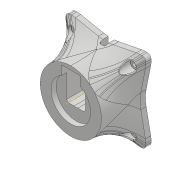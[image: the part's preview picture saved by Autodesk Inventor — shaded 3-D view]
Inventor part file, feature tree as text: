
AUTODESK INVENTOR PART (.ipt)
format: ipt  version: 2018 (Build 220112000, 112)  size: 1,944,576 bytes
history: native  units: mm
features: sketch x37, projected_geometry x36, extrude x32, fillet x13, hole x4, chamfer x4, mirror x1, other x1, revolve x1, shell x1, pattern_circular x1
ambient origin geometry x8: Origin, YZ Plane, XZ Plane, XY Plane, X Axis, Y Axis, Z Axis, Center Point
bodies: Solid1 (feature_tree)
feature tree (131):
  extrude  "Extrusion1"  Depth=45.0mm
  extrude  "Extrusion2"  Depth=2.25mm
  hole  "Hole1"  [1 undecoded]
  hole  "Hole2"  [1 undecoded]
  fillet  "Fillet1"  Radius=14.0mm
  extrude  "Extrusion3"  Depth=18.5mm
  extrude  "Extrusion4"  Depth=10.0mm
  extrude  "Extrusion5"  Depth=2.195mm
  extrude  "Extrusion6"  Depth=20.5mm
  hole  "Hole3"  [1 undecoded]
  extrude  "Extrusion7"  Depth=0.5mm
  extrude  "Extrusion8"  Depth=5.0mm TaperAngle=0.0deg
  extrude  "Extrusion9"  Depth=10.0mm
  extrude  "Extrusion10"  Depth=10.0mm
  extrude  "Extrusion11"  Depth=14.5mm
  extrude  "Extrusion12"  Depth=14.5mm
  extrude  "Extrusion13"  Depth=5.0mm
  extrude  "Extrusion14"  Depth=2.25mm
  extrude  "Extrusion15"  Depth=5.0mm
  extrude  "Extrusion16"  Depth=9.0mm
  extrude  "Extrusion17"  Depth=4.0mm
  chamfer  "Chamfer1"  Distance=1.0mm
  fillet  "Fillet7"  Radius=20.7mm
  fillet  "Fillet8"  Radius=32.0mm
  mirror  "Mirror1"
  extrude  "Extrusion18"  Depth=1.0mm TaperAngle=0.0deg
  extrude  "Extrusion19"  Depth=8.0mm
  extrude  "Extrusion20"  Depth=0.2mm TaperAngle=0.0deg
  extrude  "Extrusion21"  Depth=0.5mm TaperAngle=0.0deg
  extrude  "Extrusion22"  Depth=3.0mm TaperAngle=0.0deg
  extrude  "Extrusion23"  Depth=0.2mm TaperAngle=0.0deg
  extrude  "Extrusion24"  Depth=2.5mm TaperAngle=45.0deg
  sketch  "Sketch35"  dims[d91=8.0mm d92=0.0mm d93=3.0mm d94=0.0mm]
  other  "Work Axis1"
  revolve  "Revolution1"  [1 undecoded]
  extrude  "Extrusion25"  Depth=4.0mm TaperAngle=0.0deg
  extrude  "Extrusion26"  Depth=19.2mm TaperAngle=0.0deg
  shell  "Shell1"  Thickness=52.1mm
  extrude  "Extrusion27"  Depth=9.0mm
  extrude  "Extrusion28"  Depth=25.0mm
  chamfer  "Chamfer4"  Distance=6.9mm
  chamfer  "Chamfer5"  Distance=5.2mm
  extrude  "Extrusion29"  Depth=5.2mm
  pattern_circular  "Circular Pattern1"  [2 undecoded]
  fillet  "Fillet11"  Radius=5.0mm
  fillet  "Fillet12"  [1 undecoded]
  fillet  "Fillet13"  Radius=5.0mm
  fillet  "Fillet14"  Radius=105.0mm
  chamfer  "Chamfer6"  Distance=105.0mm
  hole  "Hole6"  [1 undecoded]
  extrude  "Extrusion30"  Depth=0.3mm
  fillet  "Fillet15"  Radius=12.8mm
  extrude  "Extrusion31"  Depth=0.3mm
  fillet  "Fillet16"  Radius=12.8mm
  extrude  "Extrusion32"  Depth=0.3mm
  fillet  "Fillet17"  Radius=20.0mm
  fillet  "Fillet18"  Radius=20.0mm
  fillet  "Fillet19"  Radius=6.0mm
  fillet  "Fillet20"  Radius=40.0mm
  sketch  "Sketch1"  dims[d0=24.5mm d1=45.0mm]
  sketch  "Sketch2"  dims[d2=1.95mm d3=0.0mm d4=2.25mm]
  projected_geometry  "Projected Loop1"
  sketch  "Sketch3"  dims[d5=20.0mm d6=2.25mm]
  projected_geometry  "Projected Loop2"
  sketch  "Sketch4"  dims[d7=5.25mm d8=5.25mm d9=14.0mm]
  projected_geometry  "Projected Loop3"
  sketch  "Sketch5"  dims[d10=5.25mm d11=18.5mm]
  projected_geometry  "Projected Loop4"
  sketch  "Sketch6"  dims[d12=10.0mm d13=0.0mm d14=20.5mm]
  projected_geometry  "Projected Loop5"
  sketch  "Sketch7"  dims[d15=2.0mm d16=2.195mm]
  projected_geometry  "Projected Loop6"
  sketch  "Sketch8"  dims[d17=2.0mm]
  projected_geometry  "Projected Loop7"
  sketch  "Sketch9"  dims[d18=2.4mm d19=6.0mm d20=4.4mm d21=2.0mm d22=90.0deg d23=8.0mm d24=20.594885mm d25=20.5mm]
  projected_geometry  "Projected Loop8"
  projected_geometry  "Projected Loop9"
  sketch  "Sketch10"  dims[d26=26.65mm d27=2.0mm]
  projected_geometry  "Projected Loop10"
  projected_geometry  "Projected Loop11"
  sketch  "Sketch11"  dims[d28=2.0mm]
  projected_geometry  "Projected Loop12"
  sketch  "Sketch12"  dims[d29=2.4mm d30=6.0mm d31=4.4mm d32=2.0mm d33=90.0deg d34=8.0mm d35=20.594885mm d36=0.5mm]
  sketch  "Sketch13"  dims[d37=18.0mm d38=5.0mm d39=0.0mm]
  sketch  "Sketch14"  dims[d41=10.0mm d42=0.0mm d43=24.5mm]
  projected_geometry  "Projected Loop13"
  sketch  "Sketch15"  dims[d44=1.15mm d45=0.0mm d46=10.0mm]
  sketch  "Sketch16"  dims[d47=21.0mm d48=14.5mm]
  projected_geometry  "Projected Loop14"
  sketch  "Sketch17"  dims[d49=20.0mm d50=14.5mm]
  projected_geometry  "Projected Loop15"
  sketch  "Sketch18"  dims[d51=24.5mm d52=5.0mm]
  projected_geometry  "Projected Loop16"
  sketch  "Sketch19"  dims[d53=5.0mm d54=2.25mm]
  projected_geometry  "Projected Loop17"
  sketch  "Sketch20"  dims[d55=2.25mm d56=5.0mm]
  projected_geometry  "Projected Loop18"
  sketch  "Sketch22"  dims[d57=5.0mm d58=9.0mm]
  sketch  "Sketch25"  dims[d59=14.75mm d60=4.0mm d61=1.0mm d62=0.0mm d63=20.7mm]
  sketch  "Sketch27"  dims[d64=2.4mm d65=6.0mm d66=4.4mm d67=2.0mm d68=90.0deg d69=8.0mm d70=20.594885mm d72=32.0mm]
  projected_geometry  "Projected Loop22"
  sketch  "Sketch28"  dims[d73=5.0mm d74=0.0mm d75=1.0mm d76=0.0mm]
  projected_geometry  "Projected Loop23"
  sketch  "Sketch29"  dims[d77=12.25mm d78=0.0mm d80=8.0mm]
  projected_geometry  "Projected Loop24"
  sketch  "Sketch30"  dims[d81=4.5mm d82=0.0mm d84=0.2mm d85=0.0mm]
  projected_geometry  "Projected Loop25"
  sketch  "Sketch33"  dims[d86=21.0mm d87=0.5mm d88=0.0mm]
  projected_geometry  "Projected Loop26"
  sketch  "Sketch36"  dims[d95=5.0mm d96=0.0mm d98=0.2mm d99=0.0mm]
  projected_geometry  "Projected Loop27"
  sketch  "Sketch37"  dims[d100=0.2mm d101=0.0mm d102=2.5mm d103=2.0mm d104=45.0deg]
  projected_geometry  "Projected Loop28"
  sketch  "Sketch38"  dims[d105=1.5mm d114=0.5mm]
  projected_geometry  "Projected Loop29"
  projected_geometry  "Projected Loop30"
  projected_geometry  "Projected Loop31"
  projected_geometry  "Projected Loop32"
  sketch  "Sketch39"  dims[d115=22.55mm d116=0.0mm d128=4.0mm d129=0.0mm]
  projected_geometry  "Projected Loop33"
  projected_geometry  "Projected Loop34"
  sketch  "Sketch40"  dims[d130=4.0mm d131=0.0mm d132=19.2mm d133=0.0mm d134=52.1mm]
  projected_geometry  "Projected Loop35"
  sketch  "Sketch41"  dims[d135=6.8mm d136=0.0mm d137=9.0mm]
  projected_geometry  "Projected Loop36"
  sketch  "Sketch42"  dims[d138=9.0mm d139=25.0mm d140=6.9mm d141=0.0mm]
  sketch  "Sketch43"  dims[d142=5.2mm]
  projected_geometry  "Projected Loop37"
  sketch  "Sketch44"  dims[d143=5.2mm d144=5.2mm d145=5.2mm d146=2.5mm d147=0.0mm d148=5.0mm d149=90.0deg d150=5.0mm d151=105.0mm d152=105.0mm d153=5.0mm d154=0.0mm d156=12.8mm d157=12.8mm d158=12.8mm d159=12.8mm d160=20.0mm d161=20.0mm d162=20.0mm d163=6.0mm d164=40.0mm d165=0.0mm d166=8.0mm d167=40.0mm d168=0.0mm d169=40.0mm d170=0.0mm d178=5.1mm d179=2.45mm d180=45.0deg d181=4.1mm d182=2.45mm d183=45.0deg d184=10.0mm d185=10.0mm d186=40.0mm d187=0.0mm d188=40.0mm d189=360.0deg d191=5.1mm d192=25.0mm d193=50.0mm d194=50.0mm d195=5.0mm d196=2.0mm d197=45.0deg d198=110.0mm d199=77.781746mm d200=77.781746mm d201=6.4mm d202=6.0mm d203=12.6mm d204=2.0mm d205=90.0deg d206=8.0mm d207=20.594885mm d208=11.0mm d209=11.0mm d210=11.0mm d211=11.0mm d212=45.0mm d213=0.0mm d214=1.0mm d215=2.0mm d216=0.0mm d217=1.5mm d218=8.0mm d219=12.0mm d220=12.0mm d221=0.0mm d222=2.0mm d223=5.0mm d224=2.0mm d225=0.3mm]
  projected_geometry  "Projected Loop38"
  projected_geometry  "Project Cut Edges1"
note: 8 required parameter values undecoded (feature->parameter linkage not recoverable at this tier; creation-order binding heuristic only, values carry confidence <= 0.55)